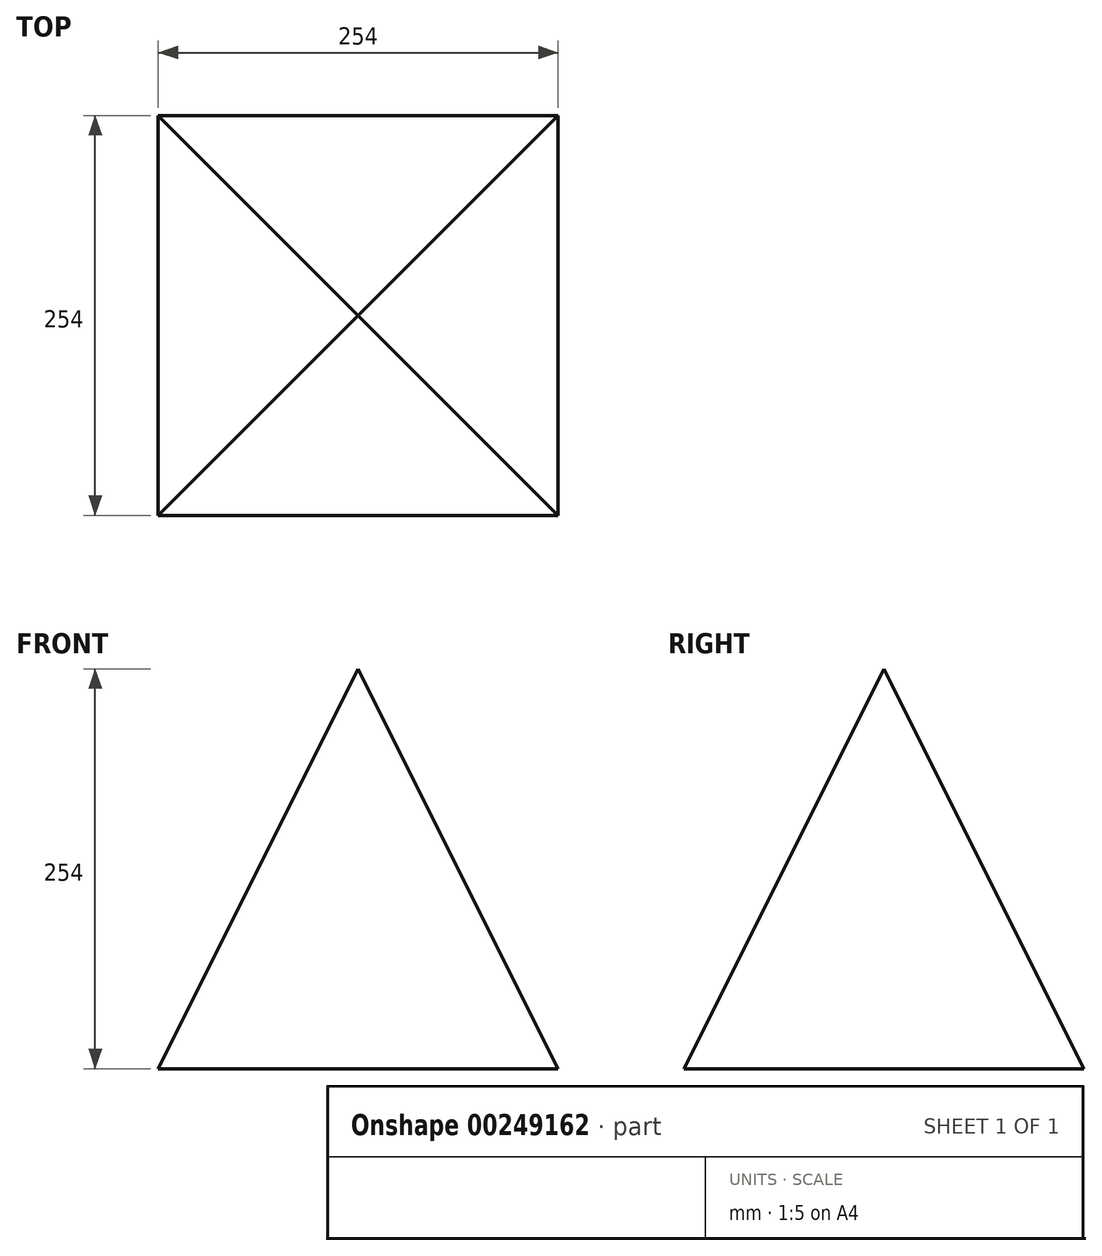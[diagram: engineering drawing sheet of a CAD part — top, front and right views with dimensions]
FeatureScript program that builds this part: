
annotation { "Feature Type Name" : "Feature", "Feature Type Description" : "" }
export const myFeature = defineFeature(function(context is Context, id is Id, definition is map)
    precondition{}
    {
        {
            var Q0;
            Q0=qCreatedBy(makeId("Front.planeOp"),FACE);
            var sketch = newSketch(context, id + "F0", { "sketchPlane" : qUnion([Q0])});
            skLineSegment(sketch, "E0.bottom", {"start": v(0, 0) * mm, "end": v(254, 0) * mm});
            skLineSegment(sketch, "E0.top", {"start": v(0, 254) * mm, "end": v(254, 254) * mm});
            skLineSegment(sketch, "E0.left", {"start": v(0, 0) * mm, "end": v(0, 254) * mm});
            skLineSegment(sketch, "E0.right", {"start": v(254, 0) * mm, "end": v(254, 254) * mm});
            skSolve(sketch);
        }
        {
            var Q0;
            Q0 = qSketchRegion(id + "F0", true);
            extrude(context, id + "F1", {"entities" : qUnion([Q0]), "depth" : 254 * mm});
        }
        {
            var Q0;
            Q0=qCreatedBy(makeId("Front.planeOp"),FACE);
            var sketch = newSketch(context, id + "F2", { "sketchPlane" : qUnion([Q0])});
            skLineSegment(sketch, "E1", {"start": v(127, 254) * mm, "end": v(0, 0) * mm});
            skLineSegment(sketch, "E2", {"start": v(0, 0) * mm, "end": v(0, 254) * mm});
            skLineSegment(sketch, "E3", {"start": v(0, 254) * mm, "end": v(127, 254) * mm});
            skSolve(sketch);
        }
        {
            var Q0;
            Q0 = qSketchRegion(id + "F2", true);
            extrude(context, id + "F6", {"entities" : qUnion([Q0]), "operationType" : NewBodyOperationType.REMOVE, "endBound" : BoundingType.UP_TO_NEXT, "depth" : 25.4 * mm});
        }
        {
            var Q0;
            Q0=qCreatedBy(makeId("Front.planeOp"),FACE);
            var sketch = newSketch(context, id + "F7", { "sketchPlane" : qUnion([Q0])});
            skLineSegment(sketch, "E4", {"start": v(127, 254) * mm, "end": v(254, 0) * mm});
            skLineSegment(sketch, "E5", {"start": v(254, 0) * mm, "end": v(254, 254) * mm});
            skLineSegment(sketch, "E6", {"start": v(254, 254) * mm, "end": v(127, 254) * mm});
            skSolve(sketch);
        }
        {
            var Q0;
            Q0 = qSketchRegion(id + "F7", true);
            extrude(context, id + "F8", {"entities" : qUnion([Q0]), "operationType" : NewBodyOperationType.REMOVE, "endBound" : BoundingType.UP_TO_NEXT, "depth" : 25.4 * mm});
        }
        {
            var Q0;
            Q0=qCreatedBy(makeId("Front.planeOp"),FACE);
            var sketch = newSketch(context, id + "F3", { "sketchPlane" : qUnion([Q0])});
            skLineSegment(sketch, "E7", {"start": v(127, 254) * mm, "end": v(254, 0) * mm});
            skLineSegment(sketch, "E8", {"start": v(254, 0) * mm, "end": v(254, 254) * mm});
            skLineSegment(sketch, "E9", {"start": v(254, 254) * mm, "end": v(127, 254) * mm});
            skSolve(sketch);
        }
        {
            var Q0;
            Q0=qCreatedBy(makeId("Right.planeOp"),FACE);
            var sketch = newSketch(context, id + "F9", { "sketchPlane" : qUnion([Q0])});
            skLineSegment(sketch, "E10", {"start": v(-254, 0) * mm, "end": v(-127, 254) * mm});
            skLineSegment(sketch, "E11", {"start": v(-127, 254) * mm, "end": v(-254, 254) * mm});
            skLineSegment(sketch, "E12", {"start": v(-254, 254) * mm, "end": v(-254, 0) * mm});
            skLineSegment(sketch, "E13", {"start": v(-127, 342.2) * mm, "end": v(-127, -52.6) * mm, "construction": true});
            skPoint(sketch, "E14.MirrorCS.end.orphan", {"position": v(0, 254) * mm});
            skPoint(sketch, "E14.MirrorCS.start.orphan", {"position": v(-127, 254) * mm});
            skPoint(sketch, "E15.MirrorCS.start.orphan", {"position": v(0, 0) * mm});
            skSolve(sketch);
        }
        {
            var Q0;
            Q0 = qSketchRegion(id + "F9", true);
            extrude(context, id + "F4", {"entities" : qUnion([Q0]), "operationType" : NewBodyOperationType.REMOVE, "depth" : 254 * mm});
        }
        {
            var Q0;
            Q0=qCreatedBy(makeId("Right.planeOp"),FACE);
            var sketch = newSketch(context, id + "F5", { "sketchPlane" : qUnion([Q0])});
            skLineSegment(sketch, "E16", {"start": v(-127, 254) * mm, "end": v(0, 0) * mm});
            skLineSegment(sketch, "E17", {"start": v(0, 0) * mm, "end": v(0, 254) * mm});
            skLineSegment(sketch, "E18", {"start": v(0, 254) * mm, "end": v(-127, 254) * mm});
            skSolve(sketch);
        }
        {
            var Q0;
            Q0 = qSketchRegion(id + "F5", true);
            extrude(context, id + "F10", {"entities" : qUnion([Q0]), "operationType" : NewBodyOperationType.REMOVE, "depth" : 254 * mm});
        }
    });
